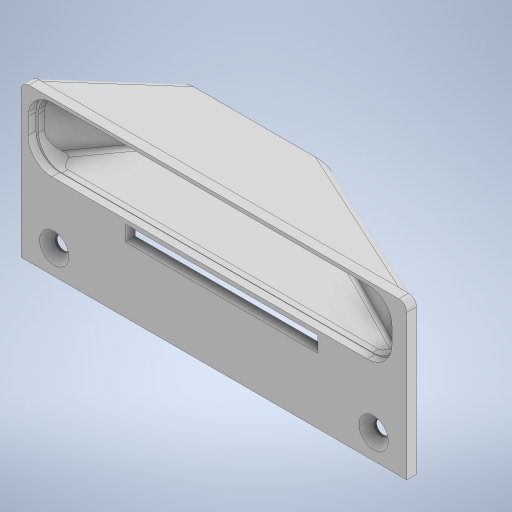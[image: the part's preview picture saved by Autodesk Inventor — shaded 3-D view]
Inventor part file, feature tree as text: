
AUTODESK INVENTOR PART (.ipt)
format: ipt  version: 2024 (Build 280153000, 153)  size: 389,632 bytes
history: native  units: in
note: dims shown in document units (in); Inventor stores cm internally (conversion verified against a paired STEP export)
features: reference x9, sketch x6, other x6, extrude x4, plane x2, loft x1, fillet x1, shell x1, chamfer x1, projected_geometry x1
ambient origin geometry x8: Origin, YZ Plane, XZ Plane, XY Plane, X Axis, Y Axis, Z Axis, Center Point
bodies: Solid1 (feature_tree)
feature tree (32):
  sketch  "Sketch1"  dims[d0=1.4472in d1=3.8976in d2=0.0in d3=0.7283in]
  plane  "Work Plane2"
  plane  "Work Plane1"
  loft  "Loft1"
  fillet  "Fillet1"  [1 undecoded]
  shell  "Shell2"  Thickness=0.7283in
  sketch  "Sketch3"  dims[d6=0.0394in d7=0.0394in]
  extrude  "Extrusion3"  Depth=0.0394in
  extrude  "Extrusion4"  Depth=0.0394in
  extrude  "Extrusion5"  Depth=0.0394in
  extrude  "Extrusion6"  Depth=0.0394in
  chamfer  "Chamfer1"  [1 undecoded]
  sketch  "Sketch2"  dims[d4=0.0394in d5=0.0394in]
  reference  "Reference1"
  reference  "Reference2"
  reference  "Reference3"
  reference  "Reference4"
  other  "Work Point1"
  sketch  "Sketch4"  dims[d8=0.0in d9=90.0deg d12=0.0787in d14=0.0394in]
  projected_geometry  "Projected Loop3"
  sketch  "Sketch5"  dims[d35=1.4472in d36=3.8976in d37=0.0in d38=0.7283in d39=0.0in d40=90.0deg d42=0.0394in]
  reference  "Reference5"
  reference  "Reference6"
  reference  "Reference7"
  reference  "Reference8"
  reference  "Reference9"
  sketch  "Sketch6"  dims[d43=0.0394in d44=0.0in d45=0.0787in d46=0.0394in d47=0.0in d48=0.0984in d49=0.0in d50=0.1378in d51=0.1378in d52=0.0in d53=0.3937in d54=0.0in d55=0.0787in d56=0.0in d57=0.0787in d58=0.0787in d59=45.0deg]
  parser-record x1  (decoder bookkeeping rows leaked as tree rows — omitted from the tree; the rows remain in map.json)
  other  "REV 3 assembly.iam"
  other  "Top3518_3668_A02_3509_A01_0204:1"
  other  "Front Hood Scoop:1"
  other  "TA07 ELECTRONICS MOUNT REV 3:1"
note: 2 required parameter values undecoded (feature->parameter linkage not recoverable at this tier; creation-order binding heuristic only, values carry confidence <= 0.55)
note: 1 file-system path scrubbed to <path> (originals preserved in map.json)
